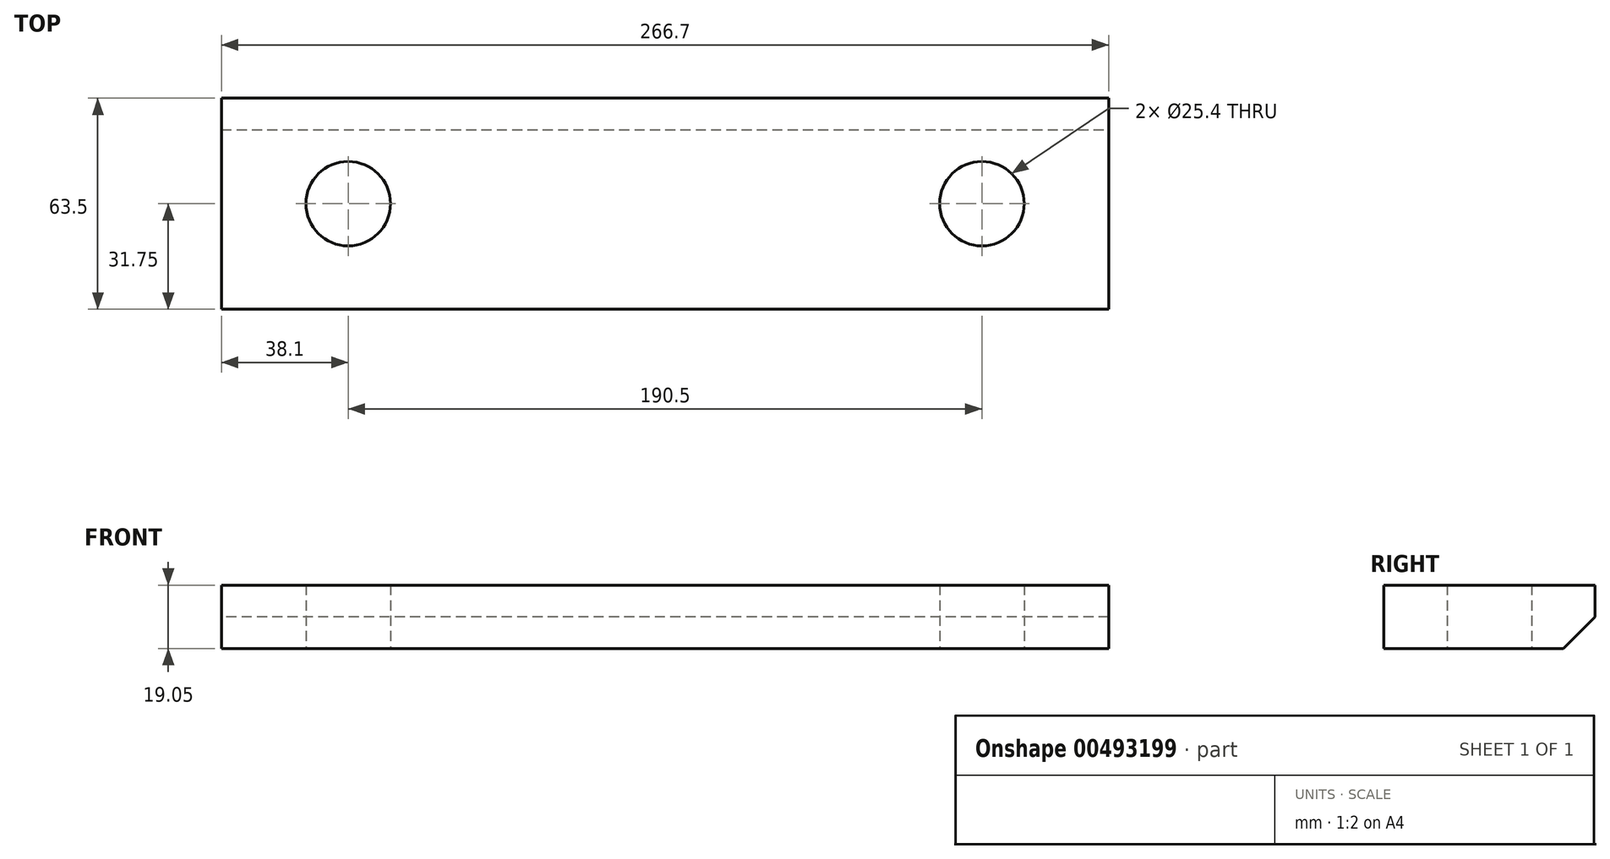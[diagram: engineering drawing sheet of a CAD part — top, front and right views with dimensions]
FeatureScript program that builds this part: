
annotation { "Feature Type Name" : "Feature", "Feature Type Description" : "" }
export const myFeature = defineFeature(function(context is Context, id is Id, definition is map)
    precondition{}
    {
        {
            var Q0;
            Q0=qCreatedBy(makeId("Top.planeOp"),FACE);
            var sketch = newSketch(context, id + "F0", { "sketchPlane" : qUnion([Q0])});
            skLineSegment(sketch, "E0.bottom", {"start": v(133.35, -31.75) * mm, "end": v(-133.35, -31.75) * mm});
            skLineSegment(sketch, "E0.top", {"start": v(133.35, 31.75) * mm, "end": v(-133.35, 31.75) * mm});
            skLineSegment(sketch, "E0.left", {"start": v(133.35, -31.75) * mm, "end": v(133.35, 31.75) * mm});
            skLineSegment(sketch, "E0.right", {"start": v(-133.35, -31.75) * mm, "end": v(-133.35, 31.75) * mm});
            skPoint(sketch, "E0.middle", {"position": v(0, 0) * mm});
            skCircle(sketch, "E1", {"center": v(-95.25, 0) * mm, "radius": 12.7 * mm});
            skCircle(sketch, "E2.MirrorC", {"center": v(95.25, 0) * mm, "radius": 12.7 * mm});
            skSolve(sketch);
        }
        {
            var Q0;
            Q0 = qSketchRegion(id + "F0", true);
            extrude(context, id + "F1", {"entities" : qUnion([Q0]), "depth" : 19.05 * mm});
        }
        {
            var Q0;
            Q0=makeQuery(id+"F1.opExtrude","CAP_EDGE",EDGE,{"disambiguationData":[OSD([sQuery(id+"F0.wireOp",EDGE,"E0.top")])],"isStart":true});
            chamfer(context, id + "F2", {"entities" : qUnion([Q0]), "width" : 9.52 * mm, "tangentPropagation" : true});
        }
    });
